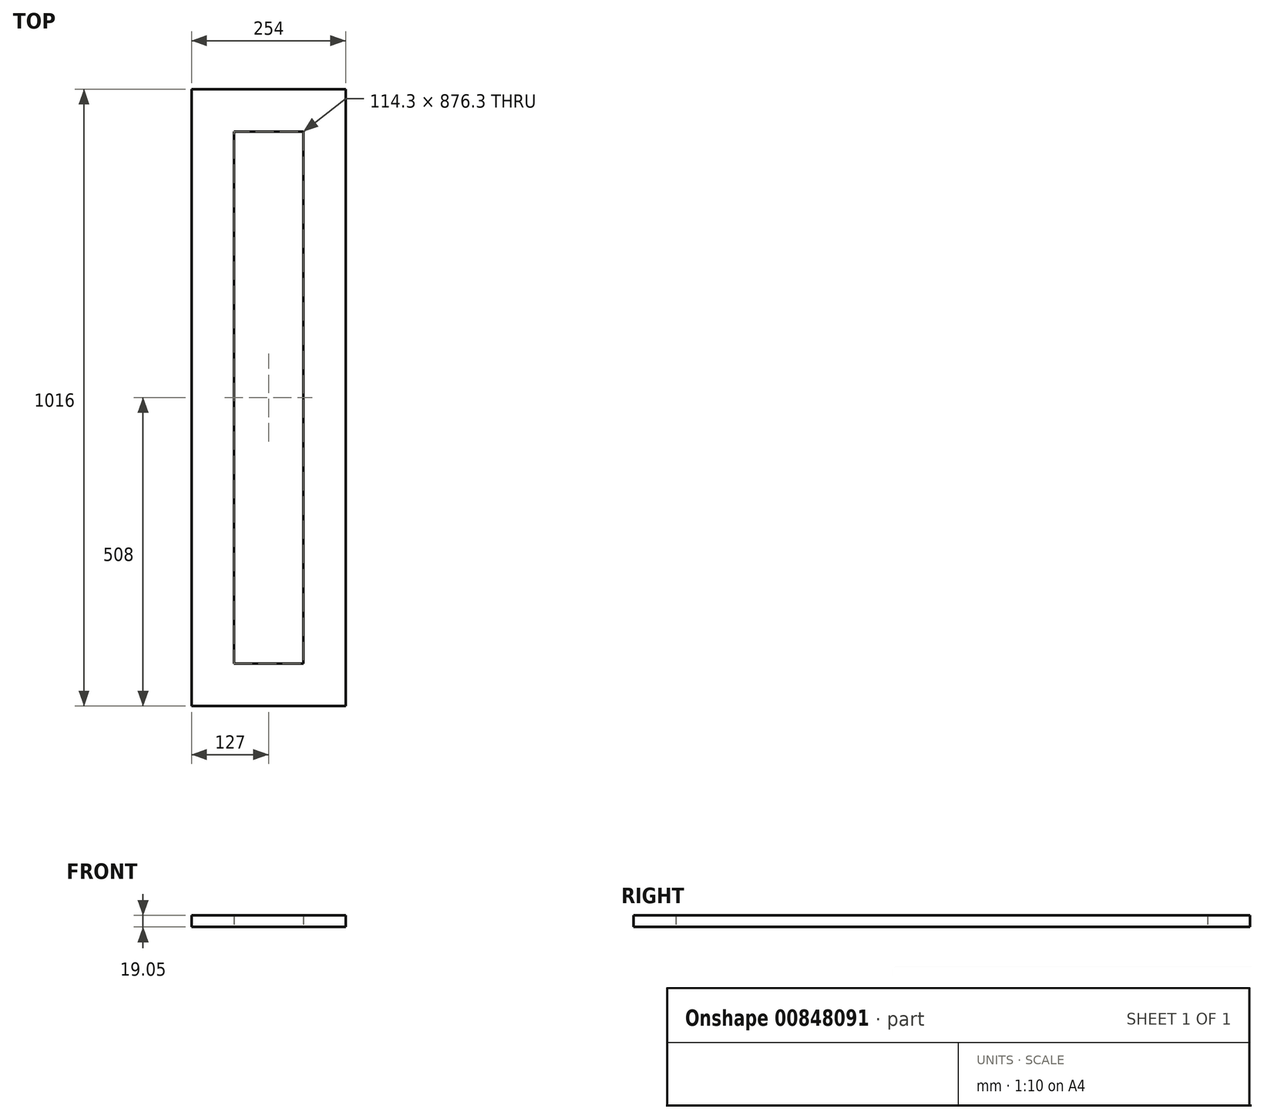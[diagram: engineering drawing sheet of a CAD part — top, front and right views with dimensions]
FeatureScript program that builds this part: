
annotation { "Feature Type Name" : "Feature", "Feature Type Description" : "" }
export const myFeature = defineFeature(function(context is Context, id is Id, definition is map)
    precondition{}
    {
        {
            var Q0;
            Q0=qCreatedBy(makeId("Top.planeOp"),FACE);
            var sketch = newSketch(context, id + "F0", { "sketchPlane" : qUnion([Q0])});
            skLineSegment(sketch, "E0.bottom", {"start": v(127, 508) * mm, "end": v(-127, 508) * mm});
            skLineSegment(sketch, "E0.top", {"start": v(127, -508) * mm, "end": v(-127, -508) * mm});
            skLineSegment(sketch, "E0.left", {"start": v(127, 508) * mm, "end": v(127, -508) * mm});
            skLineSegment(sketch, "E0.right", {"start": v(-127, 508) * mm, "end": v(-127, -508) * mm});
            skPoint(sketch, "E0.middle", {"position": v(0, 0) * mm});
            skLineSegment(sketch, "E1.bottom", {"start": v(57.15, 438.15) * mm, "end": v(-57.15, 438.15) * mm});
            skLineSegment(sketch, "E1.top", {"start": v(57.15, -438.15) * mm, "end": v(-57.15, -438.15) * mm});
            skLineSegment(sketch, "E1.left", {"start": v(57.15, 438.15) * mm, "end": v(57.15, -438.15) * mm});
            skLineSegment(sketch, "E1.right", {"start": v(-57.15, 438.15) * mm, "end": v(-57.15, -438.15) * mm});
            skSolve(sketch);
        }
        {
            var Q0;
            Q0=makeQuery(id+"F0.imprint","IMPRINT",FACE,{"disambiguationData":[TD([[makeQuery(id+"F0.imprint","IMPRINT",EDGE,{"derivedFrom":sQuery(id+"F0.wireOp",EDGE,"E0.bottom")}),1.0]])]});
            extrude(context, id + "F1", {"entities" : qUnion([Q0]), "depth" : 19.05 * mm, "offsetDistance" : 25.4 * mm});
        }
    });
